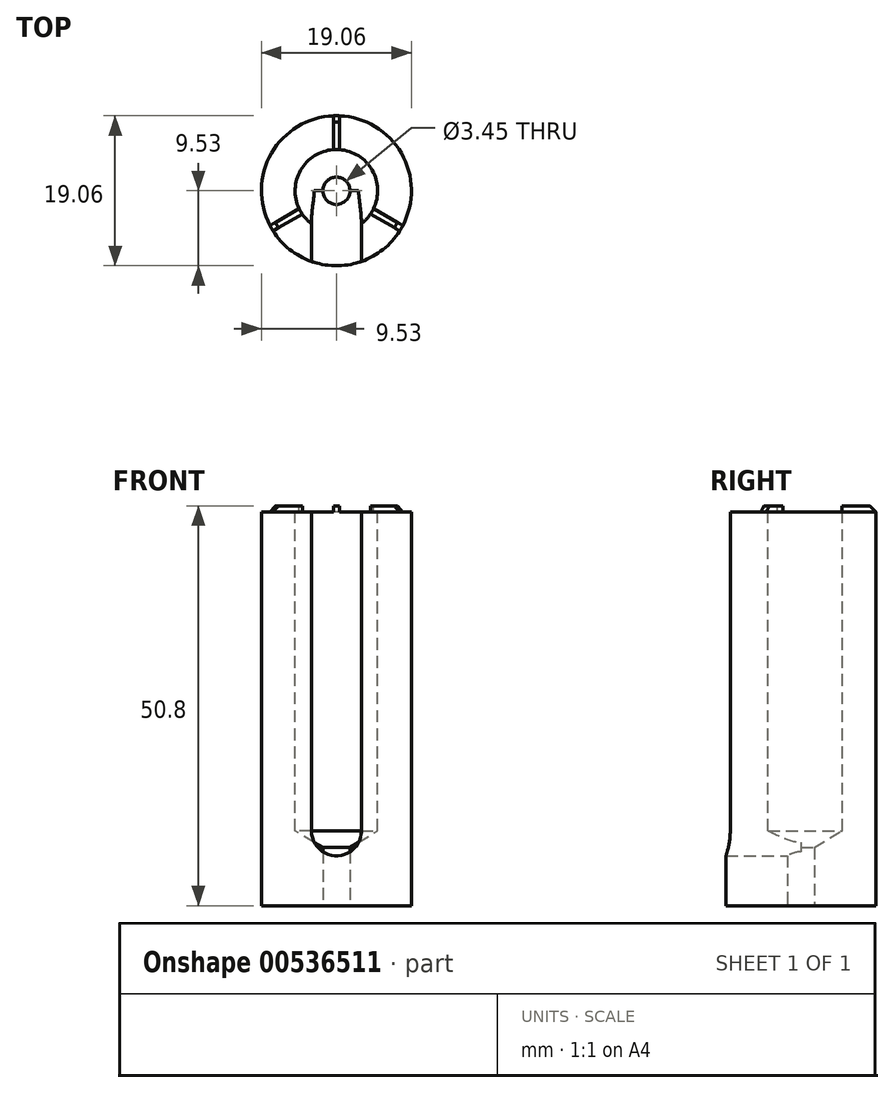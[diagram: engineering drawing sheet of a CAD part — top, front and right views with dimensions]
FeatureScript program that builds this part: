
annotation { "Feature Type Name" : "Feature", "Feature Type Description" : "" }
export const myFeature = defineFeature(function(context is Context, id is Id, definition is map)
    precondition{}
    {
        {
            var Q0;
            Q0=qCreatedBy(makeId("Top.planeOp"),FACE);
            var sketch = newSketch(context, id + "F0", { "sketchPlane" : qUnion([Q0])});
            skCircle(sketch, "E0", {"center": v(0, 0) * mm, "radius": 9.53 * mm});
            skSolve(sketch);
        }
        {
            var Q0;
            Q0 = qSketchRegion(id + "F0", true);
            extrude(context, id + "F1", {"entities" : qUnion([Q0]), "depth" : 50.8 * mm, "offsetDistance" : 25.4 * mm});
        }
        {
            var Q0;
            Q0=makeQuery(id+"F1.opExtrude","CAP_FACE",FACE,{"disambiguationData":[OSD([sQuery(id+"F0.wireOp",EDGE,"E0")])],"isStart":false});
            var sketch = newSketch(context, id + "F2", { "sketchPlane" : qUnion([Q0])});
            skPoint(sketch, "E1", {"position": v(0, 0) * mm});
            skSolve(sketch);
        }
        {
            var Q0;
            Q0=sQuery(id+"F2.wireOp",VERTEX,"E1");
            var Q1;
            Q1=makeQuery(id+"F1.opExtrude","SWEPT_BODY",BODY,{"disambiguationData":[OSD([sQuery(id+"F0.wireOp",EDGE,"E0")])]});
            hole(context, id + "F3", {"style" : HoleStyle.SIMPLE, "endStyle" : HoleEndStyle.BLIND, "standardTappedOrClearance" : lookupTablePath({ "standard" : "ANSI", "size" : "Z (0.4)", "type" : "Drilled" }), "standardBlindInLast" : lookupTablePath({ "standard" : "ANSI", "size" : "Z", "type" : "Drilled" }), "holeDiameter" : 10.5 * mm, "majorDiameter" : 6.35 * mm, "holeDepth" : 41.27 * mm, "tappedDepth" : 9.52 * mm, "tapClearance" : 1, "startFromSketch" : true, "locations" : qUnion([Q0]), "scope" : qUnion([Q1])});
        }
        {
            var Q0;
            Q0=makeQuery(id+"F1.opExtrude","CAP_FACE",FACE,{"disambiguationData":[OSD([sQuery(id+"F0.wireOp",EDGE,"E0")])],"isStart":true});
            var sketch = newSketch(context, id + "F4", { "sketchPlane" : qUnion([Q0])});
            skPoint(sketch, "E2", {"position": v(0, 0) * mm});
            skSolve(sketch);
        }
        {
            var Q0;
            Q0=sQuery(id+"F4.wireOp",VERTEX,"E2");
            var Q1;
            Q1=makeQuery(id+"F1.opExtrude","SWEPT_BODY",BODY,{"disambiguationData":[OSD([sQuery(id+"F0.wireOp",EDGE,"E0")])]});
            hole(context, id + "F5", {"style" : HoleStyle.SIMPLE, "endStyle" : HoleEndStyle.THROUGH, "standardTappedOrClearance" : lookupTablePath({ "standard" : "ANSI", "engagement" : "75%", "pitch" : "32 tpi", "size" : "#8", "type" : "Tapped" }), "standardBlindInLast" : lookupTablePath({ "standard" : "ANSI", "engagement" : "75%", "pitch" : "32 tpi", "size" : "#8", "type" : "Tapped" }), "holeDiameter" : 3.45 * mm, "majorDiameter" : 4.17 * mm, "showTappedDepth" : true, "tappedDepth" : 9.52 * mm, "tapClearance" : 1, "startFromSketch" : true, "locations" : qUnion([Q0]), "scope" : qUnion([Q1])});
        }
        {
            var Q0;
            Q0=makeQuery(id+"F1.opExtrude","CAP_FACE",FACE,{"disambiguationData":[OSD([sQuery(id+"F0.wireOp",EDGE,"E0")])],"isStart":false});
            var sketch = newSketch(context, id + "F6", { "sketchPlane" : qUnion([Q0])});
            skCircle(sketch, "E3", {"center": v(0, 0) * mm, "radius": 5.25 * mm});
            skCircle(sketch, "E4", {"center": v(0, 0) * mm, "radius": 9.53 * mm});
            skLineSegment(sketch, "E5.bottom", {"start": v(-0.4, 9.53) * mm, "end": v(0.4, 9.53) * mm});
            skLineSegment(sketch, "E5.top", {"start": v(-0.4, 5.23) * mm, "end": v(0.4, 5.23) * mm});
            skLineSegment(sketch, "E5.left", {"start": v(-0.4, 9.53) * mm, "end": v(-0.4, 5.23) * mm});
            skLineSegment(sketch, "E5.right", {"start": v(0.4, 9.53) * mm, "end": v(0.4, 5.23) * mm});
            skPoint(sketch, "E6", {"position": v(0, 9.53) * mm});
            skLineSegment(sketch, "E7.1.0", {"start": v(-8.05, -5.1) * mm, "end": v(-4.33, -2.96) * mm});
            skLineSegment(sketch, "E7.1.1", {"start": v(-8.05, -5.1) * mm, "end": v(-8.45, -4.42) * mm});
            skLineSegment(sketch, "E7.1.2", {"start": v(-8.45, -4.42) * mm, "end": v(-4.73, -2.27) * mm});
            skLineSegment(sketch, "E7.1.3", {"start": v(-4.33, -2.96) * mm, "end": v(-4.73, -2.27) * mm});
            skLineSegment(sketch, "E7.2.0", {"start": v(8.45, -4.42) * mm, "end": v(4.73, -2.27) * mm});
            skLineSegment(sketch, "E7.2.1", {"start": v(8.45, -4.42) * mm, "end": v(8.05, -5.1) * mm});
            skLineSegment(sketch, "E7.2.2", {"start": v(8.05, -5.1) * mm, "end": v(4.33, -2.96) * mm});
            skLineSegment(sketch, "E7.2.3", {"start": v(4.73, -2.27) * mm, "end": v(4.33, -2.96) * mm});
            skSolve(sketch);
        }
        {
            var Q0;
            {var subQ0=sQuery(id+"F6.wireOp",EDGE,"E5.left");var subQ5=sQuery(id+"F6.wireOp",EDGE,"E4");var subQ6=makeQuery(id+"F6.imprint","INTERSECT",VERTEX,{"derivedFrom":[subQ5,subQ0]});Q0=makeQuery(id+"F6.imprint","IMPRINT",FACE,{"disambiguationData":[TD([[makeQuery(id+"F6.imprint","IMPRINT",EDGE,{"disambiguationData":[TD([[subQ6,-1.0]])],"derivedFrom":subQ5}),1.0]])]});}
            var Q1;
            {var subQ0=sQuery(id+"F6.wireOp",EDGE,"E7.1.0");var subQ5=sQuery(id+"F6.wireOp",EDGE,"E4");var subQ6=makeQuery(id+"F6.imprint","INTERSECT",VERTEX,{"derivedFrom":[subQ5,subQ0]});Q1=makeQuery(id+"F6.imprint","IMPRINT",FACE,{"disambiguationData":[TD([[makeQuery(id+"F6.imprint","IMPRINT",EDGE,{"disambiguationData":[TD([[subQ6,-1.0]])],"derivedFrom":subQ5}),1.0]])]});}
            var Q2;
            {var subQ0=sQuery(id+"F6.wireOp",EDGE,"E5.right");var subQ5=sQuery(id+"F6.wireOp",EDGE,"E4");var subQ7=makeQuery(id+"F6.imprint","INTERSECT",VERTEX,{"derivedFrom":[subQ5,subQ0]});Q2=makeQuery(id+"F6.imprint","IMPRINT",FACE,{"disambiguationData":[TD([[makeQuery(id+"F6.imprint","IMPRINT",EDGE,{"disambiguationData":[TD([[subQ7,1.0]])],"derivedFrom":subQ5}),1.0]])]});}
            extrude(context, id + "F7", {"entities" : qUnion([Q0, Q1, Q2]), "operationType" : NewBodyOperationType.REMOVE, "oppositeDirection" : true, "depth" : 0.8 * mm, "offsetDistance" : 25.4 * mm});
        }
        {
            var Q0;
            {var subQ0=sQuery(id+"F3.hole-0.sketch.wireOp",EDGE,"core_line_2");Q0=makeQuery(id+"F7.boolean.opBoolean","SPLIT",EDGE,{"disambiguationData":[TD([makeQuery(id+"F7.opExtrude","SWEPT_FACE",FACE,{"disambiguationData":[OSD([sQuery(id+"F6.wireOp",EDGE,"E5.left")])]})])],"derivedFrom":makeQuery(id+"F3.hole-0.boolean.opBoolean","COPY",EDGE,{"derivedFrom":makeQuery(id+"F3.hole-0.opRevolve","SWEPT_EDGE",EDGE,{"disambiguationData":[OSD([subQ0,sQuery(id+"F3.hole-0.sketch.wireOp",EDGE,"core_line_3")])]})})});}
            var Q1;
            {var subQ0=sQuery(id+"F3.hole-0.sketch.wireOp",EDGE,"core_line_2");Q1=makeQuery(id+"F7.boolean.opBoolean","SPLIT",EDGE,{"disambiguationData":[TD([makeQuery(id+"F7.opExtrude","SWEPT_FACE",FACE,{"disambiguationData":[OSD([sQuery(id+"F6.wireOp",EDGE,"E7.1.0")])]})])],"derivedFrom":makeQuery(id+"F3.hole-0.boolean.opBoolean","COPY",EDGE,{"derivedFrom":makeQuery(id+"F3.hole-0.opRevolve","SWEPT_EDGE",EDGE,{"disambiguationData":[OSD([subQ0,sQuery(id+"F3.hole-0.sketch.wireOp",EDGE,"core_line_3")])]})})});}
            var Q2;
            {var subQ0=sQuery(id+"F3.hole-0.sketch.wireOp",EDGE,"core_line_2");Q2=makeQuery(id+"F7.boolean.opBoolean","SPLIT",EDGE,{"disambiguationData":[TD([makeQuery(id+"F7.opExtrude","SWEPT_FACE",FACE,{"disambiguationData":[OSD([sQuery(id+"F6.wireOp",EDGE,"E7.2.0")])]})])],"derivedFrom":makeQuery(id+"F3.hole-0.boolean.opBoolean","COPY",EDGE,{"derivedFrom":makeQuery(id+"F3.hole-0.opRevolve","SWEPT_EDGE",EDGE,{"disambiguationData":[OSD([subQ0,sQuery(id+"F3.hole-0.sketch.wireOp",EDGE,"core_line_3")])]})})});}
            var Q3;
            {var subQ0=sQuery(id+"F0.wireOp",EDGE,"E0");Q3=makeQuery(id+"F7.boolean.opBoolean","SPLIT",EDGE,{"disambiguationData":[TD([makeQuery(id+"F7.opExtrude","SWEPT_FACE",FACE,{"disambiguationData":[OSD([sQuery(id+"F6.wireOp",EDGE,"E7.2.0")])]})])],"derivedFrom":makeQuery(id+"F1.opExtrude","CAP_EDGE",EDGE,{"disambiguationData":[OSD([subQ0])],"isStart":false})});}
            var Q4;
            {var subQ0=sQuery(id+"F0.wireOp",EDGE,"E0");Q4=makeQuery(id+"F7.boolean.opBoolean","SPLIT",EDGE,{"disambiguationData":[TD([makeQuery(id+"F7.opExtrude","SWEPT_FACE",FACE,{"disambiguationData":[OSD([sQuery(id+"F6.wireOp",EDGE,"E5.left")])]})])],"derivedFrom":makeQuery(id+"F1.opExtrude","CAP_EDGE",EDGE,{"disambiguationData":[OSD([subQ0])],"isStart":false})});}
            var Q5;
            {var subQ0=sQuery(id+"F0.wireOp",EDGE,"E0");Q5=makeQuery(id+"F7.boolean.opBoolean","SPLIT",EDGE,{"disambiguationData":[TD([makeQuery(id+"F7.opExtrude","SWEPT_FACE",FACE,{"disambiguationData":[OSD([sQuery(id+"F6.wireOp",EDGE,"E7.1.0")])]})])],"derivedFrom":makeQuery(id+"F1.opExtrude","CAP_EDGE",EDGE,{"disambiguationData":[OSD([subQ0])],"isStart":false})});}
            chamfer(context, id + "F8", {"entities" : qUnion([Q0, Q1, Q2, Q3, Q4, Q5]), "width" : 0.8 * mm, "tangentPropagation" : true});
        }
        {
            var Q0;
            Q0=qCreatedBy(makeId("Front.planeOp"),FACE);
            var sketch = newSketch(context, id + "F9", { "sketchPlane" : qUnion([Q0])});
            skLineSegment(sketch, "E8.top", {"start": v(-3.18, 9.53) * mm, "end": v(3.18, 9.53) * mm, "construction": true});
            skLineSegment(sketch, "E8.left", {"start": v(-3.18, 52.55) * mm, "end": v(-3.17, 9.53) * mm});
            skLineSegment(sketch, "E8.right", {"start": v(3.18, 52.55) * mm, "end": v(3.18, 9.53) * mm});
            skArc(sketch, "E9", {"start": v(-3.18, 9.53) * mm, "mid": v(0, 6.35) * mm, "end": v(3.18, 9.53) * mm});
            skLineSegment(sketch, "E10", {"start": v(-3.18, 52.55) * mm, "end": v(3.18, 52.55) * mm, "construction": true});
            skArc(sketch, "E11", {"start": v(3.18, 52.55) * mm, "mid": v(0, 55.72) * mm, "end": v(-3.18, 52.55) * mm});
            skSolve(sketch);
        }
        {
            var Q0;
            Q0 = qSketchRegion(id + "F9", true);
            extrude(context, id + "F10", {"entities" : qUnion([Q0]), "operationType" : NewBodyOperationType.REMOVE, "depth" : 25.4 * mm, "offsetDistance" : 25.4 * mm});
        }
    });
